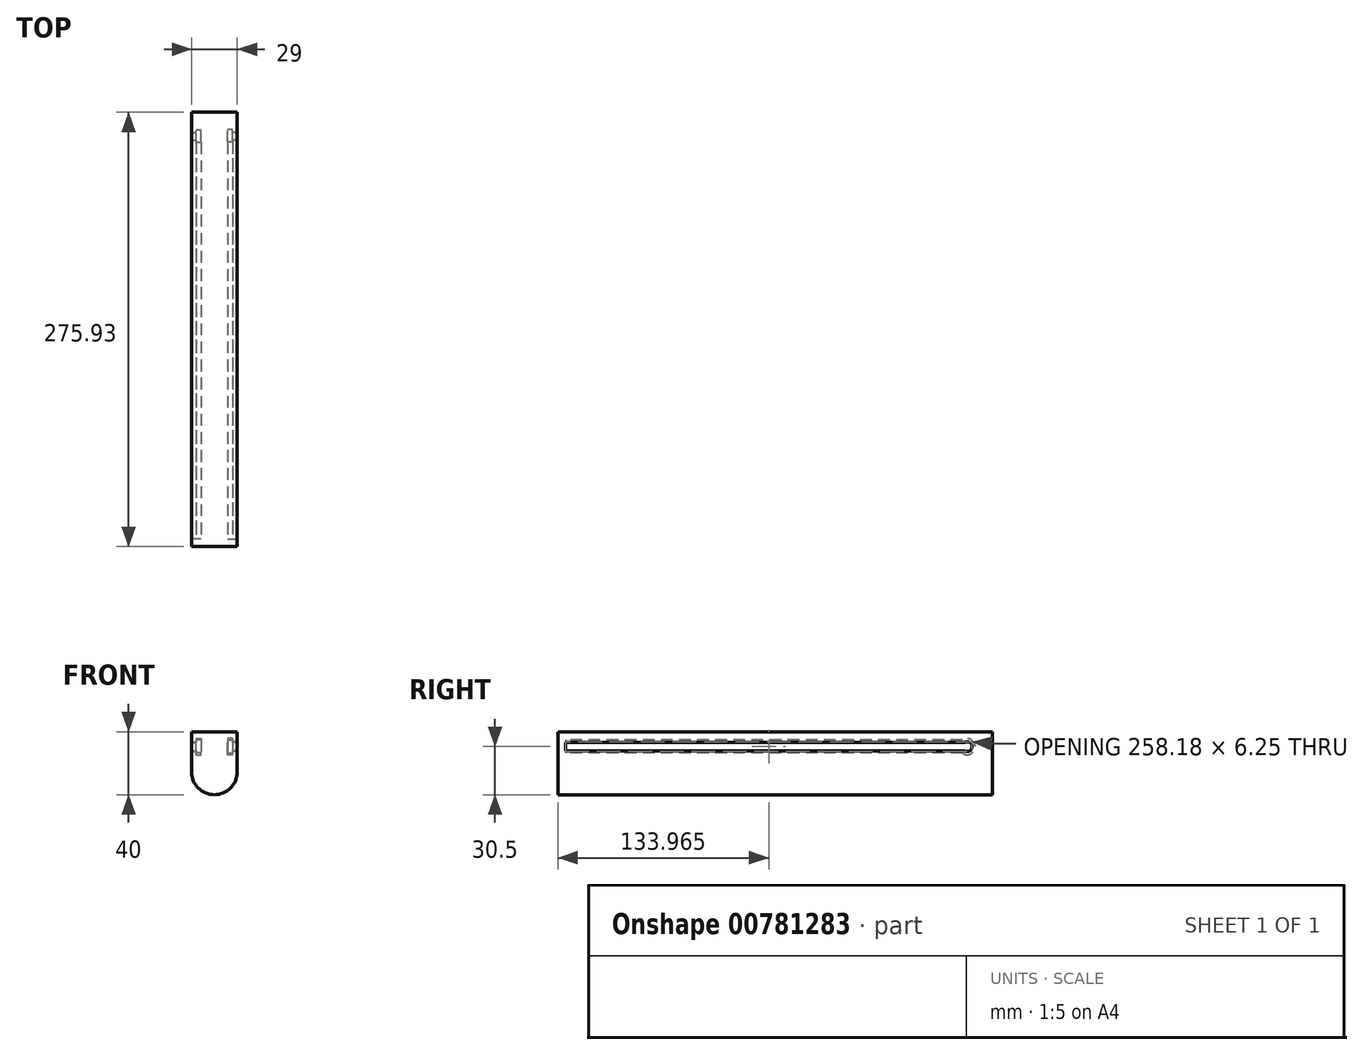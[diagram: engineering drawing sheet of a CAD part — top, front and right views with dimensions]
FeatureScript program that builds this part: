
annotation { "Feature Type Name" : "Feature", "Feature Type Description" : "" }
export const myFeature = defineFeature(function(context is Context, id is Id, definition is map)
    precondition{}
    {
        {
            var Q0;
            Q0=qCreatedBy(makeId("Front.planeOp"),FACE);
            var sketch = newSketch(context, id + "F0", { "sketchPlane" : qUnion([Q0])});
            skPoint(sketch, "E0.middle", {"position": v(0, 0) * mm});
            skLineSegment(sketch, "E1.bottom", {"start": v(0, -40) * mm, "end": v(0, -40) * mm});
            skLineSegment(sketch, "E2", {"start": v(-14.5, -25.5) * mm, "end": v(-14.5, 0) * mm});
            skLineSegment(sketch, "E3", {"start": v(-14.5, 0) * mm, "end": v(14.5, 0) * mm});
            skLineSegment(sketch, "E4", {"start": v(14.5, 0) * mm, "end": v(14.5, -25.5) * mm});
            skPoint(sketch, "E5.visualSharp", {"position": v(-14.5, -40) * mm});
            skArc(sketch, "E5.filletArc", {"start": v(-14.5, -25.5) * mm, "mid": v(-10.25, -35.75) * mm, "end": v(0, -40) * mm});
            skPoint(sketch, "E6.visualSharp", {"position": v(14.5, -40) * mm});
            skArc(sketch, "E6.filletArc", {"start": v(0, -40) * mm, "mid": v(10.25, -35.75) * mm, "end": v(14.5, -25.5) * mm});
            skSolve(sketch);
        }
        {
            var Q0;
            Q0 = qSketchRegion(id + "F0", true);
            extrude(context, id + "F1", {"entities" : qUnion([Q0]), "oppositeDirection" : true, "depth" : ((515.86 / 2) + 18) * mm, "offsetDistance" : 25 * mm});
        }
        {
            var Q0;
            Q0=qCreatedBy(makeId("Front.planeOp"),FACE);
            var sketch = newSketch(context, id + "F2", { "sketchPlane" : qUnion([Q0])});
            skPoint(sketch, "E7.middle", {"position": v(0, 0) * mm});
            skLineSegment(sketch, "E8", {"start": v(0, 3.5) * mm, "end": v(0, -4.5) * mm});
            skLineSegment(sketch, "E9", {"start": v(0, -4.5) * mm, "end": v(-3, -4.5) * mm});
            skLineSegment(sketch, "E10", {"start": v(0, 3.5) * mm, "end": v(-3, 3.5) * mm});
            skLineSegment(sketch, "E11", {"start": v(-3, 3.5) * mm, "end": v(-3, 2) * mm});
            skLineSegment(sketch, "E12", {"start": v(-3, -3) * mm, "end": v(-3, -4.5) * mm});
            skLineSegment(sketch, "E13", {"start": v(-3, 2) * mm, "end": v(-8, 2) * mm});
            skLineSegment(sketch, "E14", {"start": v(-8, 2) * mm, "end": v(-8, -3) * mm});
            skLineSegment(sketch, "E15", {"start": v(-8, -3) * mm, "end": v(-3, -3) * mm});
            skLineSegment(sketch, "E16", {"start": v(-3, 2) * mm, "end": v(-3, -3) * mm, "construction": true});
            skSolve(sketch);
        }
        {
            var Q0;
            Q0=makeQuery(id+"F2.imprint","IMPRINT",FACE,{"disambiguationData":[TD([[makeQuery(id+"F2.imprint","IMPRINT",EDGE,{"derivedFrom":sQuery(id+"F2.wireOp",EDGE,"E8")}),-1.0]])]});
            extrude(context, id + "F3", {"entities" : qUnion([Q0]), "oppositeDirection" : true, "depth" : ((515.86 / 2) - 2) * mm, "offsetDistance" : 25 * mm});
        }
        {
            var Q0;
            Q0=makeQuery(id+"F3.opExtrude","SWEPT_BODY",BODY,{"disambiguationData":[OSD([sQuery(id+"F2.wireOp",EDGE,"E8"),sQuery(id+"F2.wireOp",EDGE,"E9"),sQuery(id+"F2.wireOp",EDGE,"E10"),sQuery(id+"F2.wireOp",EDGE,"E11"),sQuery(id+"F2.wireOp",EDGE,"E12"),sQuery(id+"F2.wireOp",EDGE,"E13"),sQuery(id+"F2.wireOp",EDGE,"E14"),sQuery(id+"F2.wireOp",EDGE,"E15")])]});
            transform(context, id + "F4", {"entities" : qUnion([Q0]), "transformType" : TransformType.TRANSLATION_3D, "dx" : -8.5 * mm, "dy" : 5 * mm, "dz" : -9 * mm, "makeCopy" : false});
        }
        {
            var Q0;
            Q0=qCreatedBy(makeId("Front.planeOp"),FACE);
            var sketch = newSketch(context, id + "F5", { "sketchPlane" : qUnion([Q0])});
            skPoint(sketch, "E17.middle", {"position": v(0, 0) * mm});
            skLineSegment(sketch, "E18", {"start": v(0, 5) * mm, "end": v(0, -5) * mm});
            skLineSegment(sketch, "E19", {"start": v(0, -5) * mm, "end": v(3, -5) * mm});
            skLineSegment(sketch, "E20", {"start": v(3, -5) * mm, "end": v(3, -3) * mm});
            skLineSegment(sketch, "E21", {"start": v(3, 3) * mm, "end": v(3, 5) * mm});
            skLineSegment(sketch, "E22", {"start": v(3, 5) * mm, "end": v(0, 5) * mm});
            skLineSegment(sketch, "E23", {"start": v(3, 3) * mm, "end": v(8, 3) * mm});
            skLineSegment(sketch, "E24", {"start": v(3, -3) * mm, "end": v(8, -3) * mm});
            skLineSegment(sketch, "E25", {"start": v(8, -3) * mm, "end": v(8, 3) * mm});
            skLineSegment(sketch, "E26", {"start": v(3, 3) * mm, "end": v(3, -3) * mm, "construction": true});
            skLineSegment(sketch, "E27", {"start": v(0, 0) * mm, "end": v(3, 0) * mm});
            skLineSegment(sketch, "E28", {"start": v(3, 0) * mm, "end": v(8, 0) * mm});
            skSolve(sketch);
        }
        {
            var Q0;
            Q0=makeQuery(id+"F5.imprint","IMPRINT",FACE,{"disambiguationData":[TD([[makeQuery(id+"F5.imprint","IMPRINT",EDGE,{"derivedFrom":sQuery(id+"F5.wireOp",EDGE,"E21")}),1.0]])]});
            var Q1;
            Q1=sQuery(id+"F5.wireOp",EDGE,"E27");
            revolve(context, id + "F6", {"surfaceOperationType" : NewSurfaceOperationType.NEW, "entities" : qUnion([Q0]), "axis" : qUnion([Q1]), "revolveType" : RevolveType.FULL});
        }
        {
            var Q0;
            Q0=makeQuery(id+"F6.opRevolve","SWEPT_BODY",BODY,{"disambiguationData":[OSD([sQuery(id+"F5.wireOp",EDGE,"E18"),sQuery(id+"F5.wireOp",EDGE,"E21"),sQuery(id+"F5.wireOp",EDGE,"E22"),sQuery(id+"F5.wireOp",EDGE,"E23"),sQuery(id+"F5.wireOp",EDGE,"E25"),sQuery(id+"F5.wireOp",EDGE,"E27"),sQuery(id+"F5.wireOp",EDGE,"E28")])]});
            transform(context, id + "F7", {"entities" : qUnion([Q0]), "transformType" : TransformType.TRANSLATION_3D, "dx" : 8.5 * mm, "dy" : ((515.86 / 2) + 2) * mm, "dz" : -9.5 * mm, "makeCopy" : false});
        }
        {
            var Q0;
            Q0=makeQuery(id+"F3.opExtrude","SWEPT_BODY",BODY,{"disambiguationData":[OSD([sQuery(id+"F2.wireOp",EDGE,"E8"),sQuery(id+"F2.wireOp",EDGE,"E9"),sQuery(id+"F2.wireOp",EDGE,"E10"),sQuery(id+"F2.wireOp",EDGE,"E11"),sQuery(id+"F2.wireOp",EDGE,"E12"),sQuery(id+"F2.wireOp",EDGE,"E13"),sQuery(id+"F2.wireOp",EDGE,"E14"),sQuery(id+"F2.wireOp",EDGE,"E15")])]});
            var Q1;
            Q1=makeQuery(id+"F6.opRevolve","SWEPT_BODY",BODY,{"disambiguationData":[OSD([sQuery(id+"F5.wireOp",EDGE,"E18"),sQuery(id+"F5.wireOp",EDGE,"E21"),sQuery(id+"F5.wireOp",EDGE,"E22"),sQuery(id+"F5.wireOp",EDGE,"E23"),sQuery(id+"F5.wireOp",EDGE,"E25"),sQuery(id+"F5.wireOp",EDGE,"E27"),sQuery(id+"F5.wireOp",EDGE,"E28")])]});
            var Q2;
            Q2=qCreatedBy(makeId("Right.planeOp"),FACE);
            mirror(context, id + "F8", {"entities" : qUnion([Q0, Q1]), "mirrorPlane" : qUnion([Q2])});
        }
        {
            var Q0;
            Q0=makeQuery(id+"F8.opPattern","COPY",BODY,{"derivedFrom":makeQuery(id+"F3.opExtrude","SWEPT_BODY",BODY,{"disambiguationData":[OSD([sQuery(id+"F2.wireOp",EDGE,"E8"),sQuery(id+"F2.wireOp",EDGE,"E9"),sQuery(id+"F2.wireOp",EDGE,"E10"),sQuery(id+"F2.wireOp",EDGE,"E11"),sQuery(id+"F2.wireOp",EDGE,"E12"),sQuery(id+"F2.wireOp",EDGE,"E13"),sQuery(id+"F2.wireOp",EDGE,"E14"),sQuery(id+"F2.wireOp",EDGE,"E15")])]}),"instanceName":"1"});
            var Q1;
            Q1=makeQuery(id+"F3.opExtrude","SWEPT_BODY",BODY,{"disambiguationData":[OSD([sQuery(id+"F2.wireOp",EDGE,"E8"),sQuery(id+"F2.wireOp",EDGE,"E9"),sQuery(id+"F2.wireOp",EDGE,"E10"),sQuery(id+"F2.wireOp",EDGE,"E11"),sQuery(id+"F2.wireOp",EDGE,"E12"),sQuery(id+"F2.wireOp",EDGE,"E13"),sQuery(id+"F2.wireOp",EDGE,"E14"),sQuery(id+"F2.wireOp",EDGE,"E15")])]});
            var Q2;
            Q2=makeQuery(id+"F6.opRevolve","SWEPT_BODY",BODY,{"disambiguationData":[OSD([sQuery(id+"F5.wireOp",EDGE,"E18"),sQuery(id+"F5.wireOp",EDGE,"E21"),sQuery(id+"F5.wireOp",EDGE,"E22"),sQuery(id+"F5.wireOp",EDGE,"E23"),sQuery(id+"F5.wireOp",EDGE,"E25"),sQuery(id+"F5.wireOp",EDGE,"E27"),sQuery(id+"F5.wireOp",EDGE,"E28")])]});
            var Q3;
            Q3=makeQuery(id+"F8.opPattern","COPY",BODY,{"derivedFrom":makeQuery(id+"F6.opRevolve","SWEPT_BODY",BODY,{"disambiguationData":[OSD([sQuery(id+"F5.wireOp",EDGE,"E18"),sQuery(id+"F5.wireOp",EDGE,"E21"),sQuery(id+"F5.wireOp",EDGE,"E22"),sQuery(id+"F5.wireOp",EDGE,"E23"),sQuery(id+"F5.wireOp",EDGE,"E25"),sQuery(id+"F5.wireOp",EDGE,"E27"),sQuery(id+"F5.wireOp",EDGE,"E28")])]}),"instanceName":"1"});
            var Q4;
            Q4=makeQuery(id+"F1.opExtrude","SWEPT_BODY",BODY,{"disambiguationData":[OSD([sQuery(id+"F0.wireOp",EDGE,"E2"),sQuery(id+"F0.wireOp",EDGE,"E3"),sQuery(id+"F0.wireOp",EDGE,"E4"),sQuery(id+"F0.wireOp",EDGE,"E5.filletArc"),sQuery(id+"F0.wireOp",EDGE,"E6.filletArc")])]});
            booleanBodies(context, id + "F9", {"operationType" : BooleanOperationType.SUBTRACTION, "tools" : qUnion([Q0, Q1, Q2, Q3]), "targets" : qUnion([Q4]), "offset" : true, "offsetAll" : true, "offsetDistance" : .125 * mm});
        }
    });
